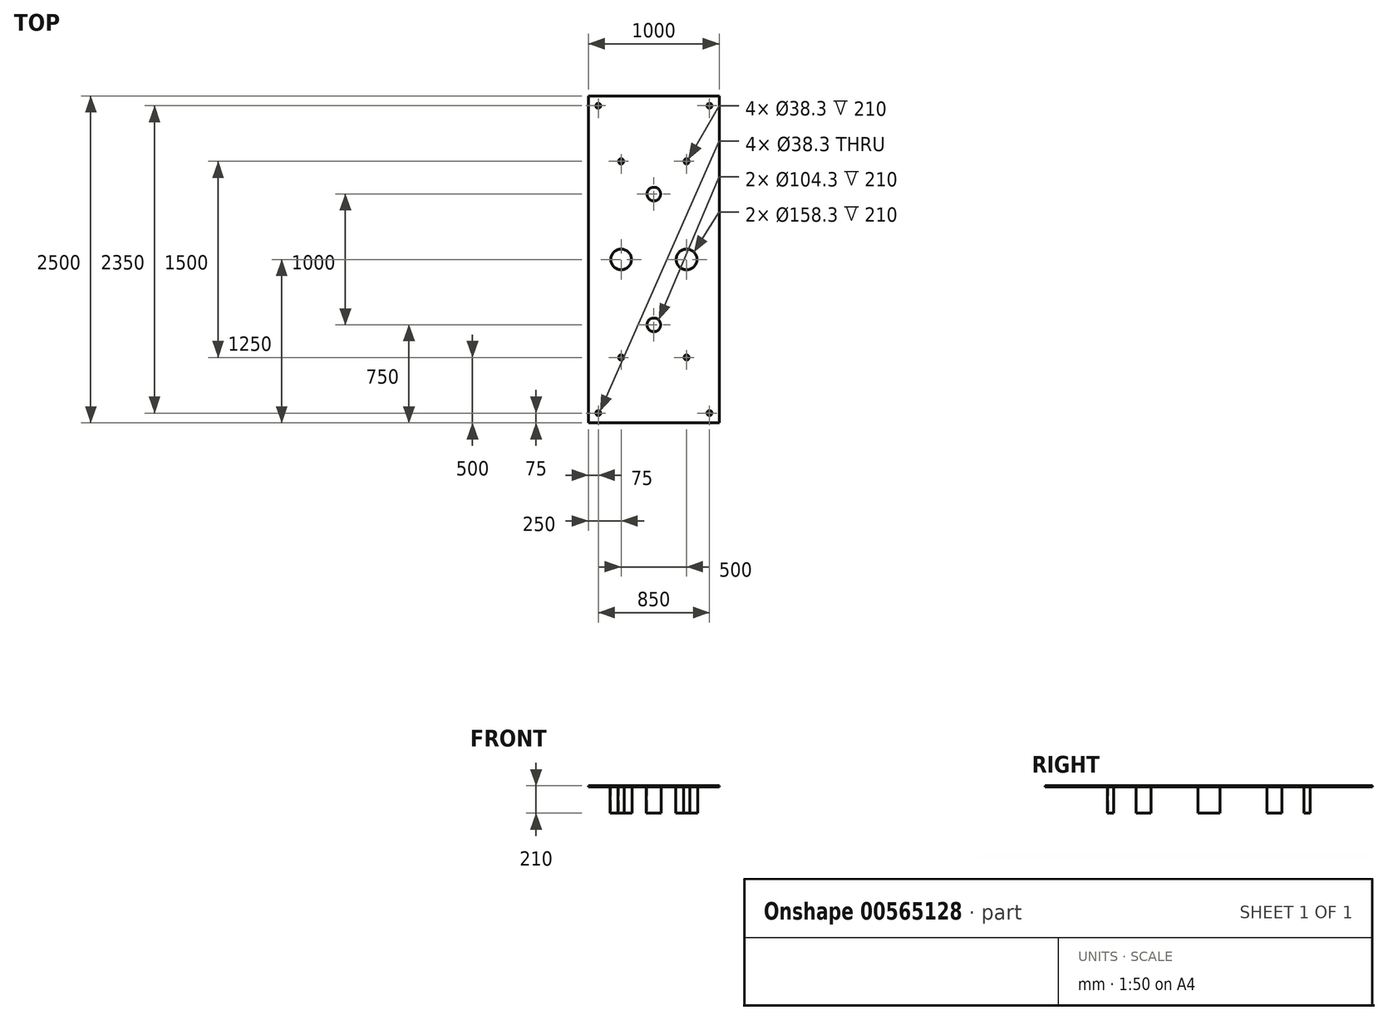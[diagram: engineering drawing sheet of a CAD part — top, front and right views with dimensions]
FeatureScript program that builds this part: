
annotation { "Feature Type Name" : "Feature", "Feature Type Description" : "" }
export const myFeature = defineFeature(function(context is Context, id is Id, definition is map)
    precondition{}
    {
        {
            var Q0;
            Q0=qCreatedBy(makeId("Top.planeOp"),FACE);
            var sketch = newSketch(context, id + "F0", { "sketchPlane" : qUnion([Q0])});
            skLineSegment(sketch, "E0.bottom", {"start": v(-500, 1250) * mm, "end": v(500, 1250) * mm});
            skLineSegment(sketch, "E0.top", {"start": v(-500, -1250) * mm, "end": v(500, -1250) * mm});
            skLineSegment(sketch, "E0.left", {"start": v(-500, 1250) * mm, "end": v(-500, -1250) * mm});
            skLineSegment(sketch, "E0.right", {"start": v(500, 1250) * mm, "end": v(500, -1250) * mm});
            skCircle(sketch, "E1", {"center": v(250, -750) * mm, "radius": 19.15 * mm});
            skCircle(sketch, "E2", {"center": v(-250, -750) * mm, "radius": 19.15 * mm});
            skCircle(sketch, "E3", {"center": v(0, -500) * mm, "radius": 52.15 * mm});
            skCircle(sketch, "E4", {"center": v(0, 500) * mm, "radius": 52.15 * mm});
            skCircle(sketch, "E5", {"center": v(250, 0) * mm, "radius": 79.15 * mm});
            skCircle(sketch, "E6", {"center": v(-250, 0) * mm, "radius": 79.15 * mm});
            skCircle(sketch, "E7", {"center": v(-250, 750) * mm, "radius": 19.15 * mm});
            skCircle(sketch, "E8", {"center": v(250, 750) * mm, "radius": 19.15 * mm});
            skCircle(sketch, "E9", {"center": v(425, 1175) * mm, "radius": 19.15 * mm});
            skCircle(sketch, "E10", {"center": v(-425, 1175) * mm, "radius": 19.15 * mm});
            skCircle(sketch, "E11", {"center": v(425, -1175) * mm, "radius": 19.15 * mm});
            skCircle(sketch, "E12", {"center": v(-425, -1175) * mm, "radius": 19.15 * mm});
            skSolve(sketch);
        }
        {
            var Q0;
            Q0=makeQuery(id+"F0.imprint","IMPRINT",FACE,{"disambiguationData":[TD([[makeQuery(id+"F0.imprint","IMPRINT",EDGE,{"derivedFrom":sQuery(id+"F0.wireOp",EDGE,"E0.bottom")}),-1.0]])]});
            extrude(context, id + "F1", {"entities" : qUnion([Q0]), "depth" : 10 * mm, "offsetDistance" : 25 * mm});
        }
        {
            var Q0;
            Q0=makeQuery(id+"F1.opExtrude","CAP_FACE",FACE,{"disambiguationData":[OSD([sQuery(id+"F0.wireOp",EDGE,"E0.bottom"),sQuery(id+"F0.wireOp",EDGE,"E0.top"),sQuery(id+"F0.wireOp",EDGE,"E0.left"),sQuery(id+"F0.wireOp",EDGE,"E0.right"),sQuery(id+"F0.wireOp",EDGE,"E1"),sQuery(id+"F0.wireOp",EDGE,"E2"),sQuery(id+"F0.wireOp",EDGE,"E3"),sQuery(id+"F0.wireOp",EDGE,"E4"),sQuery(id+"F0.wireOp",EDGE,"E5"),sQuery(id+"F0.wireOp",EDGE,"E6"),sQuery(id+"F0.wireOp",EDGE,"E7"),sQuery(id+"F0.wireOp",EDGE,"E8")])],"isStart":true});
            var sketch = newSketch(context, id + "F2", { "sketchPlane" : qUnion([Q0])});
            skLineSegment(sketch, "E13", {"start": v(0, 967.14) * mm, "end": v(0, -985.92) * mm, "construction": true});
            skLineSegment(sketch, "E14", {"start": v(422.54, 0) * mm, "end": v(-403.76, 0) * mm, "construction": true});
            skLineSegment(sketch, "E15", {"start": v(408.45, 750) * mm, "end": v(-403.76, 750) * mm, "construction": true});
            skLineSegment(sketch, "E16", {"start": v(190.14, 500) * mm, "end": v(-220.66, 500) * mm, "construction": true});
            skLineSegment(sketch, "E17", {"start": v(169.01, -500) * mm, "end": v(-220.66, -500) * mm, "construction": true});
            skLineSegment(sketch, "E18", {"start": v(384.98, -750) * mm, "end": v(-356.8, -750) * mm, "construction": true});
            skLineSegment(sketch, "E19", {"start": v(250, 974.93) * mm, "end": v(250, -882.87) * mm, "construction": true});
            skLineSegment(sketch, "E20", {"start": v(-250, 991.46) * mm, "end": v(-250, -956.05) * mm, "construction": true});
            skCircle(sketch, "E21", {"center": v(250, 750) * mm, "radius": 24 * mm});
            skCircle(sketch, "E22", {"center": v(250, 750) * mm, "radius": 19.15 * mm});
            skCircle(sketch, "E23", {"center": v(-250, 750) * mm, "radius": 19.15 * mm});
            skCircle(sketch, "E24", {"center": v(-250, 750) * mm, "radius": 24 * mm});
            skCircle(sketch, "E25", {"center": v(0, 500) * mm, "radius": 57.15 * mm});
            skCircle(sketch, "E26", {"center": v(0, 500) * mm, "radius": 52.15 * mm});
            skCircle(sketch, "E27", {"center": v(250, 0) * mm, "radius": 84.15 * mm});
            skCircle(sketch, "E28", {"center": v(250, 0) * mm, "radius": 79.15 * mm});
            skCircle(sketch, "E29", {"center": v(-250, 0) * mm, "radius": 79.15 * mm});
            skCircle(sketch, "E30", {"center": v(0, -500) * mm, "radius": 57.15 * mm});
            skCircle(sketch, "E31", {"center": v(0, -500) * mm, "radius": 52.15 * mm});
            skCircle(sketch, "E32", {"center": v(250, -750) * mm, "radius": 24 * mm});
            skCircle(sketch, "E33", {"center": v(250, -750) * mm, "radius": 19.15 * mm});
            skCircle(sketch, "E34", {"center": v(-250, -750) * mm, "radius": 24 * mm});
            skCircle(sketch, "E35", {"center": v(-250, -750) * mm, "radius": 19.15 * mm});
            skCircle(sketch, "E36", {"center": v(-250, 0) * mm, "radius": 84.15 * mm});
            skSolve(sketch);
        }
        {
            var Q0;
            Q0=makeQuery(id+"F2.imprint","IMPRINT",FACE,{"disambiguationData":[TD([[makeQuery(id+"F2.imprint","IMPRINT",EDGE,{"derivedFrom":sQuery(id+"F2.wireOp",EDGE,"E29")}),1.0]])]});
            var Q1;
            Q1=makeQuery(id+"F2.imprint","IMPRINT",FACE,{"disambiguationData":[TD([[makeQuery(id+"F2.imprint","IMPRINT",EDGE,{"derivedFrom":sQuery(id+"F2.wireOp",EDGE,"E25")}),1.0]])]});
            var Q2;
            Q2=makeQuery(id+"F2.imprint","IMPRINT",FACE,{"disambiguationData":[TD([[makeQuery(id+"F2.imprint","IMPRINT",EDGE,{"derivedFrom":sQuery(id+"F2.wireOp",EDGE,"E23")}),1.0]])]});
            var Q3;
            Q3=makeQuery(id+"F2.imprint","IMPRINT",FACE,{"disambiguationData":[TD([[makeQuery(id+"F2.imprint","IMPRINT",EDGE,{"derivedFrom":sQuery(id+"F2.wireOp",EDGE,"E21")}),1.0]])]});
            var Q4;
            Q4=makeQuery(id+"F2.imprint","IMPRINT",FACE,{"disambiguationData":[TD([[makeQuery(id+"F2.imprint","IMPRINT",EDGE,{"derivedFrom":sQuery(id+"F2.wireOp",EDGE,"E27")}),1.0]])]});
            var Q5;
            Q5=makeQuery(id+"F2.imprint","IMPRINT",FACE,{"disambiguationData":[TD([[makeQuery(id+"F2.imprint","IMPRINT",EDGE,{"derivedFrom":sQuery(id+"F2.wireOp",EDGE,"E30")}),1.0]])]});
            var Q6;
            Q6=makeQuery(id+"F2.imprint","IMPRINT",FACE,{"disambiguationData":[TD([[makeQuery(id+"F2.imprint","IMPRINT",EDGE,{"derivedFrom":sQuery(id+"F2.wireOp",EDGE,"E32")}),1.0]])]});
            var Q7;
            Q7=makeQuery(id+"F2.imprint","IMPRINT",FACE,{"disambiguationData":[TD([[makeQuery(id+"F2.imprint","IMPRINT",EDGE,{"derivedFrom":sQuery(id+"F2.wireOp",EDGE,"E34")}),1.0]])]});
            extrude(context, id + "F3", {"entities" : qUnion([Q0, Q1, Q2, Q3, Q4, Q5, Q6, Q7]), "operationType" : NewBodyOperationType.ADD, "depth" : 200 * mm, "offsetDistance" : 25 * mm});
        }
    });
